FCSTD DOCUMENT  (FreeCAD 0.18R16146 (Git))
Label: YDriveGegenlager_Ver2
License: All rights reserved
LicenseURL: http://en.wikipedia.org/wiki/All_rights_reserved
objects: Part::Cut×19, Part::Cylinder×9, Part::Box×7, Part::Feature×4, Part::Fillet×2
note: 41 computed .brp shape members not serialized (recipe doc carries the construction recipe); baked Part::Feature solids carry a one-line shape summary decoded from their .brp

FEATURE [Part::Cylinder] Cylinder020  label="M"
  Angle = 360
  AttacherType = Attacher::AttachEngine3D
  Height = 40
  Placement = pos=(27,55.8,0) rot=(0,0,1;0rad)
  Radius = 6
FEATURE [Part::Cylinder] Cylinder021  label="Z1"
  Angle = 360
  AttacherType = Attacher::AttachEngine3D
  Height = 40
  Placement = pos=(15,15,0) rot=(0,0,1;0rad)
  Radius = 4.1
FEATURE [Part::Cylinder] Cylinder022  label="Z2"
  Angle = 360
  AttacherType = Attacher::AttachEngine3D
  Height = 40
  Placement = pos=(15,96.6,0) rot=(0,0,1;0rad)
  Radius = 4.1
FEATURE [Part::Box] Box005  label="H1"
  AttacherType = Attacher::AttachEngine3D
  Height = 40
  Length = 15.7
  Placement = pos=(50.9,14.9,0) rot=(0,0,1;0rad)
  Width = 15.7
FEATURE [Part::Box] Box007  label="H2"
  AttacherType = Attacher::AttachEngine3D
  Height = 40
  Length = 15.7
  Placement = pos=(50.9,81,0) rot=(0,0,1;0rad)
  Width = 15.7
FEATURE [Part::Box] Box  label="Würfel"
  AttacherType = Attacher::AttachEngine3D
  Height = 14
  Length = 74
  Width = 111.6
FEATURE [Part::Cylinder] Cylinder  label="Zylinder"
  Angle = 360
  AttacherType = Attacher::AttachEngine3D
  Height = 30
  Placement = pos=(-30,55.8,0) rot=(0,0,1;0rad)
  Radius = 48
FEATURE [Part::Cut] Cut
  Base = -> Box
  Tool = -> Cylinder
FEATURE [Part::Cylinder] Cylinder023  label="Zylinder001"
  Angle = 360
  AttacherType = Attacher::AttachEngine3D
  Height = 30
  Placement = pos=(87,55.8,0) rot=(0,0,1;0rad)
  Radius = 25
FEATURE [Part::Cut] Cut001
  Base = -> Cut
  Tool = -> Cylinder023
FEATURE [Part::Fillet] Fillet
  Base = -> Cut001
  Edges = 4 edges r=10: [Edge4,Edge22,Edge24,Edge25]
FEATURE [Part::Cut] Cut002
  Base = -> Fillet
  Tool = -> Cylinder020
FEATURE [Part::Box] Box008  label="Würfel001"
  AttacherType = Attacher::AttachEngine3D
  Height = 30
  Length = 3
  Placement = pos=(16,17,0) rot=(0,0,-1;1.36136rad)
  Width = 40
FEATURE [Part::Box] Box009  label="Würfel002"
  AttacherType = Attacher::AttachEngine3D
  Height = 30
  Length = 3
  Placement = pos=(55,86.5,0) rot=(0,0,1;1.36136rad)
  Width = 40
FEATURE [Part::Cylinder] Cylinder024  label="Zylinder002"
  Angle = 360
  AttacherType = Attacher::AttachEngine3D
  Height = 40
  Placement = pos=(34,40,7) rot=(1,0,0;1.5708rad)
  Radius = 2.6
FEATURE [Part::Cylinder] Cylinder025  label="Zylinder003"
  Angle = 360
  AttacherType = Attacher::AttachEngine3D
  Height = 40
  Placement = pos=(34,111.6,7) rot=(1,0,0;1.5708rad)
  Radius = 2.6
FEATURE [Part::Cylinder] Cylinder026  label="Zylinder004"
  Angle = 360
  AttacherType = Attacher::AttachEngine3D
  Height = 10
  Placement = pos=(34,111.6,7) rot=(1,0,0;1.5708rad)
  Radius = 4.5
FEATURE [Part::Cylinder] Cylinder027  label="Zylinder005"
  Angle = 360
  AttacherType = Attacher::AttachEngine3D
  Height = 10
  Placement = pos=(34,10,7) rot=(1,0,0;1.5708rad)
  Radius = 4.5
FEATURE [Part::Box] Box010  label="Würfel003"
  AttacherType = Attacher::AttachEngine3D
  Height = 20
  Length = 8.4
  Placement = pos=(29.8,30,3.2) rot=(0,0,1;0rad)
  Width = 5
FEATURE [Part::Box] Box011  label="Würfel004"
  AttacherType = Attacher::AttachEngine3D
  Height = 20
  Length = 8.4
  Placement = pos=(29.8,76,3.2) rot=(0,0,1;0rad)
  Width = 5
FEATURE [Part::Cut] Cut003
  Base = -> Cut002
  Tool = -> Box007
FEATURE [Part::Cut] Cut004
  Base = -> Cut003
  Tool = -> Box005
FEATURE [Part::Cut] Cut005
  Base = -> Cut004
  Tool = -> Cylinder022
FEATURE [Part::Cut] Cut006
  Base = -> Cut005
  Tool = -> Cylinder021
FEATURE [Part::Cut] Cut007
  Base = -> Cut006
  Tool = -> Box008
FEATURE [Part::Cut] Cut008
  Base = -> Cut007
  Tool = -> Box009
FEATURE [Part::Cut] Cut009
  Base = -> Cut008
  Tool = -> Box011
FEATURE [Part::Cut] Cut010
  Base = -> Cut009
  Tool = -> Box010
FEATURE [Part::Cut] Cut011
  Base = -> Cut010
  Tool = -> Cylinder027
FEATURE [Part::Cut] Cut012
  Base = -> Cut011
  Tool = -> Cylinder024
FEATURE [Part::Cut] Cut013
  Base = -> Cut012
  Tool = -> Cylinder026
FEATURE [Part::Cut] Cut014
  Base = -> Cut013
  Tool = -> Cylinder025
FEATURE [Part::Fillet] Fillet001
  Base = -> Cut014
  Edges = 28 edges r=0.4: [Edge1,Edge4,Edge5,Edge6,Edge7,Edge8,Edge9,Edge10,Edge11,Edge12,Edge13,Edge14,Edge15,Edge16,Edge17,Edge42,Edge45,Edge46,Edge47,Edge48,Edge49,Edge50,Edge51,Edge52,Edge53,Edge54,Edge55,Edge64]
FEATURE [Part::Feature] Part__Feature  label="ScrewTap-M4x70_"
  Placement = pos=(20,30,40) rot=(0,0,1;0rad)
  shape: bbox 5.739 x 6.156 x 72.1 mm, 410 faces (baked)
FEATURE [Part::Feature] Part__Feature001  label="ScrewTap-M4x70_001"
  Placement = pos=(40,10,40) rot=(0,0,1;0rad)
  shape: bbox 5.739 x 6.156 x 72.1 mm, 410 faces (baked)
FEATURE [Part::Feature] Part__Feature002  label="ScrewTap-M4x70_002"
  Placement = pos=(20,81.6,40) rot=(0,0,1;0rad)
  shape: bbox 5.739 x 6.156 x 72.1 mm, 410 faces (baked)
FEATURE [Part::Feature] Part__Feature003  label="ScrewTap-M4x70_003"
  Placement = pos=(40,101.6,40) rot=(0,0,1;0rad)
  shape: bbox 5.739 x 6.156 x 72.1 mm, 410 faces (baked)
FEATURE [Part::Cut] Cut015
  Base = -> Fillet001
  Tool = -> Part__Feature
FEATURE [Part::Cut] Cut016
  Base = -> Cut015
  Tool = -> Part__Feature003
FEATURE [Part::Cut] Cut017
  Base = -> Cut016
  Tool = -> Part__Feature002
FEATURE [Part::Cut] Cut018
  Base = -> Cut017
  Tool = -> Part__Feature001
